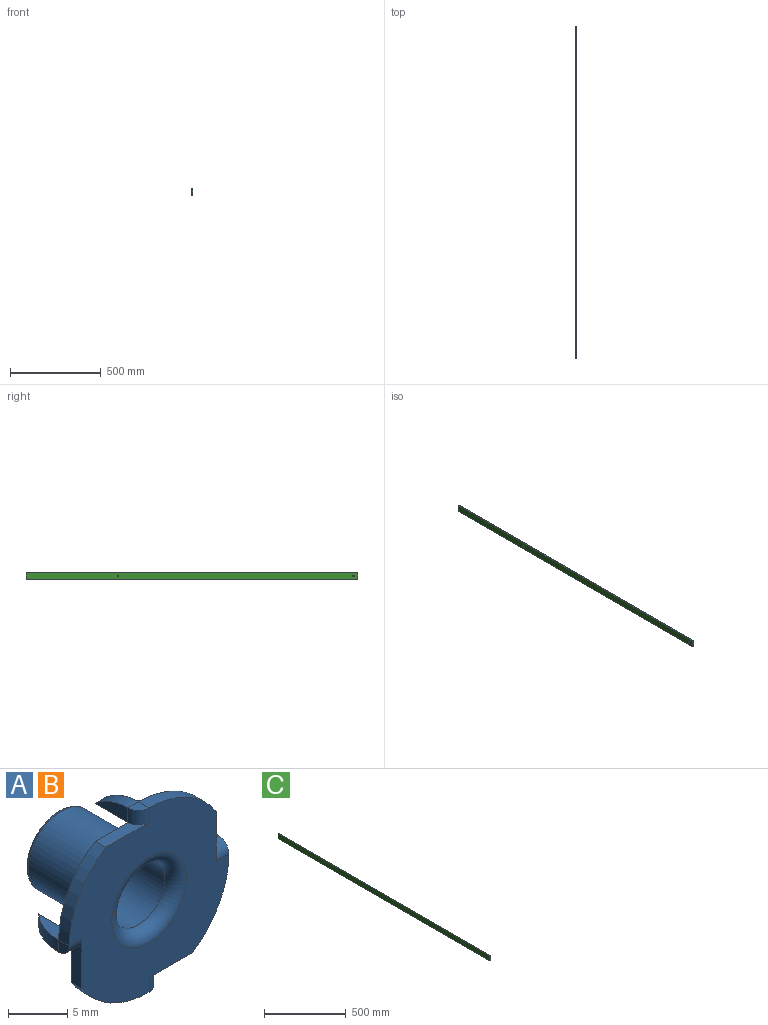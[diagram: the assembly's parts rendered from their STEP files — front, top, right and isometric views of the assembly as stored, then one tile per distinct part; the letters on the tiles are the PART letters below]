
ASSEMBLY  parts=3 mates=1
PART A: 48 faces, bbox 19.1x10.8x19.1 mm
  f0: cone r=2.35mm half-angle=45deg, axis (0,1,0), area 3.7mm2, adj f40,f47
  f1: plane 19.04x19.04mm, normal (0,1,0), area 205.1mm2, adj f2,f3,f4,f5,f6,f7,f9,f10
  f2: plane 1.27x0.03mm, normal (0,0,-1), area 0mm2, adj f1,f8,f14,f35
  f3: plane 1.27x0.03mm, normal (1,0,0), area 0mm2, adj f1,f8,f13,f29
  f4: plane 1.27x0.03mm, normal (0,0,1), area 0mm2, adj f1,f8,f12,f23
  f5: plane 1.27x0.03mm, normal (-1,0,0), area 0mm2, adj f1,f8,f11,f16
  f6: cylinder r=9.53mm len=8.01mm, axis (0,-1,0), area 12.1mm2, adj f1,f8,f14,f27,f31,f44
  f7: cylinder r=9.53mm len=8.01mm, axis (0,-1,0), area 12.1mm2, adj f1,f8,f11,f33
  f8: plane 19.05x19.05mm, normal (0,-1,0), area 201.7mm2, adj f2,f3,f4,f5,f6,f7,f9,f10
  f9: cylinder r=9.53mm len=8.01mm, axis (0,-1,0), area 12.1mm2, adj f1,f8,f13,f21,f25,f45
  f10: cylinder r=9.53mm len=8.01mm, axis (0,-1,0), area 12.1mm2, adj f1,f8,f12,f15,f18,f46
  f11: plane 5.16x1.27mm, normal (0,0,1), area 6.6mm2, adj f1,f5,f7,f8
  f12: plane 5.16x1.27mm, normal (1,0,0), area 6.6mm2, adj f1,f4,f8,f10
  f13: plane 5.16x1.27mm, normal (0,0,-1), area 6.6mm2, adj f1,f3,f8,f9
  f14: plane 5.16x1.27mm, normal (-1,0,0), area 6.6mm2, adj f1,f2,f6,f8
  f15: plane 1.27x1.27mm, normal (0,0,1), area 1.3mm2, adj f10,f17,f18
  f16: plane 5.16x1.59mm, normal (0,0,-1), area 6.2mm2, adj f1,f5,f17,f18,f19,f20,f46
  f17: cylinder r=1.27mm len=1.49mm, axis (0,0,1), area 3mm2, adj f8,f15,f16,f19
  f18: cylinder r=5.81mm len=3.89mm, axis (1,0,0), area 5.4mm2, adj f10,f15,f16,f19,f20,f46
  f19: plane 3.89x1.49mm, normal (-1,0,0), area 4mm2, adj f16,f17,f18
  f20: plane 3.57x1.48mm, normal (1,0,0), area 3.5mm2, adj f16,f18,f46
  f21: plane 1.27x1.27mm, normal (1,0,0), area 1.3mm2, adj f9,f22,f25
  f22: cylinder r=1.27mm len=1.49mm, axis (1,0,0), area 3mm2, adj f8,f21,f23,f24
  f23: plane 5.16x1.59mm, normal (-1,0,0), area 6.2mm2, adj f1,f4,f22,f24,f25,f26,f45
  f24: plane 3.89x1.49mm, normal (0,0,1), area 4mm2, adj f22,f23,f25
  f25: cylinder r=5.81mm len=3.89mm, axis (0,0,-1), area 5.4mm2, adj f9,f21,f23,f24,f26,f45
  f26: plane 3.57x1.48mm, normal (0,0,-1), area 3.5mm2, adj f23,f25,f45
  f27: plane 1.27x1.27mm, normal (0,0,-1), area 1.3mm2, adj f6,f28,f31
  f28: cylinder r=1.27mm len=1.49mm, axis (0,0,-1), area 3mm2, adj f8,f27,f29,f30
  f29: plane 5.16x1.59mm, normal (0,0,1), area 6.2mm2, adj f1,f3,f28,f30,f31,f32,f44
  f30: plane 3.89x1.49mm, normal (1,0,0), area 4mm2, adj f28,f29,f31
  f31: cylinder r=5.81mm len=3.89mm, axis (-1,0,0), area 5.4mm2, adj f6,f27,f29,f30,f32,f44
  f32: plane 3.57x1.48mm, normal (-1,0,0), area 3.5mm2, adj f29,f31,f44
  f33: plane 1.27x1.27mm, normal (-1,0,0), area 1.3mm2, adj f7,f34,f37
  f34: cylinder r=1.27mm len=1.49mm, axis (-1,0,0), area 3mm2, adj f8,f33,f35,f36
  f35: plane 5.16x1.27mm, normal (1,0,0), area 6.2mm2, adj f2,f34,f36,f37,f38
  f36: plane 3.89x1.49mm, normal (0,0,-1), area 4mm2, adj f34,f35,f37
  f37: cylinder r=5.81mm len=3.89mm, axis (0,0,1), area 5.4mm2, adj f33,f35,f36,f38
  f38: plane 3.89x1.49mm, normal (0,0,1), area 4mm2, adj f1,f35,f37
  f39: cylinder r=3.95mm len=8.89mm, axis (0,-1,0), area 220.6mm2, adj f42,f43
  f40: plane 7.26x7.26mm, normal (0,1,0), area 7.2mm2, adj f0,f42
  f41: torus R=4.45mm, axis (0,1,0), area 45.6mm2, adj f8,f47
  f42: torus R=3.63mm, axis (0,1,0), area 12mm2, adj f39,f40
  f43: torus R=4.27mm, axis (0,1,0), area 12.7mm2, adj f1,f39
  f44: cylinder r=0.32mm len=1.49mm, axis (0,0,1), area 0.7mm2, adj f1,f6,f29,f31,f32
  f45: cylinder r=0.32mm len=1.49mm, axis (-1,0,0), area 0.7mm2, adj f1,f9,f23,f25,f26
  f46: cylinder r=0.32mm len=1.49mm, axis (0,0,1), area 0.7mm2, adj f1,f10,f16,f18,f20
  f47: cylinder r=3.17mm len=9.4mm, axis (0,1,0), area 187.5mm2, adj f0,f41
PART B: same geometry as A
PART C: 6 faces, bbox 6.4x1828.8x38.1 mm
  f0: plane 1828.8x38.1mm, normal (1,0,0), area 69677.3mm2, adj f1,f3,f4,f5
  f1: plane 1828.8x6.35mm, normal (0,0,1), area 11612.9mm2, adj f0,f2,f4,f5
  f2: plane 1828.8x38.1mm, normal (-1,0,0), area 69677.3mm2, adj f1,f3,f4,f5
  f3: plane 1828.8x6.35mm, normal (0,0,-1), area 11612.9mm2, adj f0,f2,f4,f5
  f4: plane 38.1x6.35mm, normal (0,-1,0), area 241.9mm2, adj f0,f1,f2,f3
  f5: plane 38.1x6.35mm, normal (0,1,0), area 241.9mm2, adj f0,f1,f2,f3
PLACE A rot(axis=(-0.58,0.58,0.58),120deg) t=(4.44,406.4,0)mm
PLACE B rot(axis=(-0.58,0.58,0.58),120deg) t=(4.44,-889,0)mm
PLACE C at identity fixed
MATE fastened B.f0 <-> C.f0  axis (-1,0,0) through (3.17,-889,0)mm
